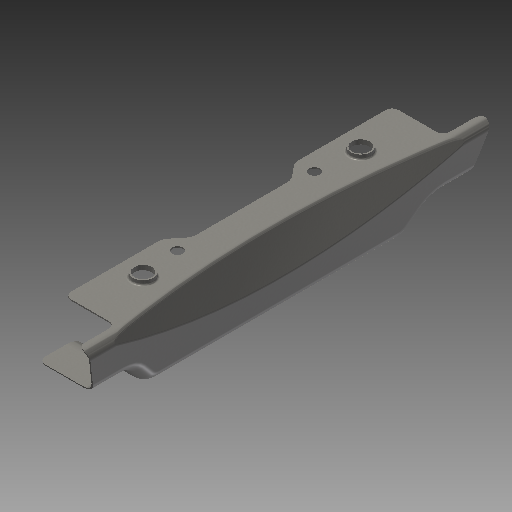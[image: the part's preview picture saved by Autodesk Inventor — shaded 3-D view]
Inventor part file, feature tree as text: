
AUTODESK INVENTOR PART (.ipt)
format: ipt  version: 2019 (Build 230136000, 136)  size: 513,536 bytes
history: native  units: mm
features: sketch x10, fillet x9, extrude x8, mirror x1, plane x1, revolve x1, shell x1, hole x1, projected_geometry x1
ambient origin geometry x8: Origin, YZ Plane, XZ Plane, XY Plane, X Axis, Y Axis, Z Axis, Center Point
bodies: Solid1 (feature_tree)
feature tree (33):
  extrude  "Extrusion1"  Depth=14.018127mm
  extrude  "Extrusion2"  Depth=56.350953mm
  mirror  "Mirror1"
  plane  "Work Plane1"
  revolve  "Revolution1"  [1 undecoded]
  fillet  "Fillet1"  Radius=37.871812mm
  fillet  "Fillet2"  Radius=315.0mm
  fillet  "Fillet3"  Radius=100.194916mm
  fillet  "Fillet4"  Radius=118.184297mm
  shell  "Shell1"  Thickness=20.439428mm
  extrude  "Extrusion3"  Depth=326.0mm TaperAngle=0.0deg
  extrude  "Extrusion4"  TaperAngle=90.0deg  [1 undecoded]
  fillet  "Fillet5"  Radius=767.023979mm
  extrude  "Extrusion5"  Depth=10.0mm
  fillet  "Fillet6"  Radius=6.0mm
  fillet  "Fillet7"  Radius=3.0mm
  extrude  "Extrusion6"  Depth=326.0mm TaperAngle=0.0deg
  extrude  "Extrusion7"  Depth=5.0mm
  extrude  "Extrusion8"  Depth=128.0mm
  fillet  "Fillet8"  Radius=5.0mm
  fillet  "Fillet9"  Radius=1.0mm
  hole  "Hole1"  [1 undecoded]
  sketch  "Sketch1"  dims[d0=42.630458mm d1=14.018127mm]
  sketch  "Sketch2"  dims[d2=13.730888mm d4=56.350953mm]
  sketch  "Sketch3"  dims[d5=56.328722mm d6=37.871811mm d8=37.871812mm d9=315.0mm d10=0.0mm d11=100.194916mm d12=118.184297mm d13=20.439428mm]
  sketch  "Sketch4"  dims[d14=147.009066mm d15=326.0mm d16=0.0mm]
  sketch  "Sketch5"  dims[d17=1600.0mm d19=90.0deg d20=767.023979mm]
  sketch  "Sketch6"  dims[d21=16.0mm d22=10.0mm d23=6.0mm d24=3.0mm]
  sketch  "Sketch7"  dims[d25=1.0mm d26=326.0mm d27=0.0mm]
  sketch  "Sketch8"  dims[d28=326.0mm d29=0.0mm d30=5.0mm]
  sketch  "Sketch9"  dims[d31=128.0mm d32=128.0mm d33=5.0mm d34=1.0mm d35=0.0mm]
  sketch  "Sketch10"  dims[d36=5.0mm d37=5.0mm d38=10.5mm d39=8.726646mm d40=8.726646mm d41=78.0mm d42=3.0mm d43=10.0mm d44=5.0mm d45=85.0mm d46=85.0mm d47=19.470068mm d48=19.470068mm d49=13.8mm d50=13.8mm d51=1.0mm d52=0.0mm d53=15.8mm d54=15.8mm d55=3.5mm d56=0.0mm d57=1.5mm d58=3.0mm d59=15.8mm d60=15.8mm d61=3.5mm d62=0.0mm d63=107.0mm d64=24.0mm d65=8.5mm d66=6.0mm d67=4.0mm d68=2.0mm d69=90.0deg d70=2.0mm d71=20.594885mm]
  projected_geometry  "Project Cut Edges1"
note: 3 required parameter values undecoded (feature->parameter linkage not recoverable at this tier; creation-order binding heuristic only, values carry confidence <= 0.55)